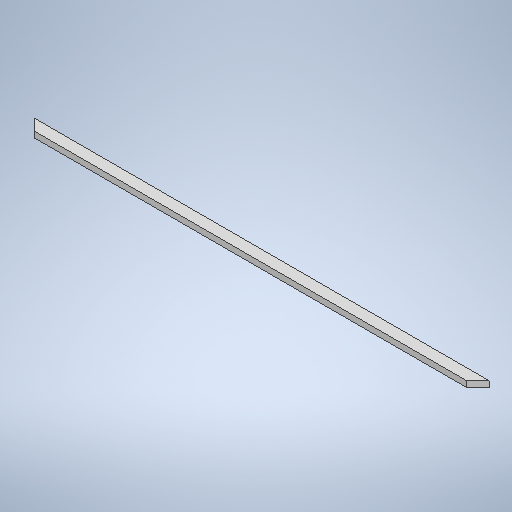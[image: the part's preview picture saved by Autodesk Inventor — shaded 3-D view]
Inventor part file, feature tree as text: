
AUTODESK INVENTOR PART (.ipt)
format: ipt  version: 2025.1 (Build 291241000, 241)  size: 264,704 bytes
history: native  units: mm
features: extrude x2, sketch x2, projected_geometry x1
ambient origin geometry x8: Origin, YZ Plane, XZ Plane, XY Plane, X Axis, Y Axis, Z Axis, Center Point
bodies: Solid1 (feature_tree)
feature tree (5):
  extrude  "Extrusion1"  Depth=19.0mm
  extrude  "Extrusion2"  Depth=10.0mm TaperAngle=0.0deg
  sketch  "Sketch1"  dims[d0=19.0mm d1=770.0mm]
  sketch  "Sketch2"  dims[d2=10.0mm d3=0.0mm d5=10.0mm d6=0.0mm d8=45.0deg]
  projected_geometry  "Projected Loop1"
